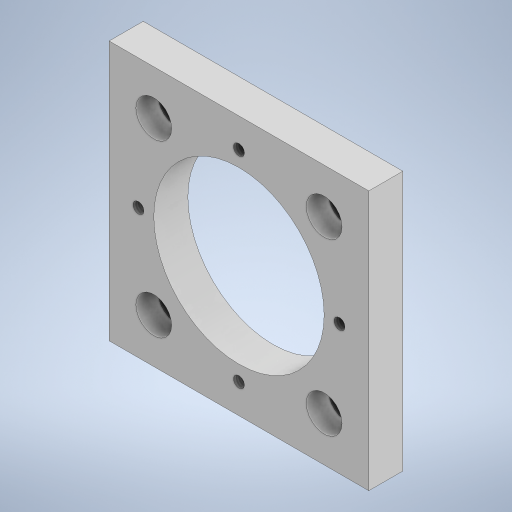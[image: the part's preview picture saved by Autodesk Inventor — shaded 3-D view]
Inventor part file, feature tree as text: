
AUTODESK INVENTOR PART (.ipt)
format: ipt  version: 2023 (Build 270158000, 158)  size: 272,896 bytes
history: native  units: mm
features: sketch x3, hole x2, projected_geometry x2, extrude x1
ambient origin geometry x8: Origin, YZ Plane, XZ Plane, XY Plane, X Axis, Y Axis, Z Axis, Center Point
bodies: Solid1 (feature_tree)
feature tree (8):
  extrude  "Extrusion1"  Depth=76.2mm
  hole  "Hole1"  [1 undecoded]
  hole  "Hole2"  [1 undecoded]
  sketch  "Sketch1"  dims[d0=76.2mm d1=76.2mm]
  sketch  "Sketch2"  dims[d2=10.0mm d3=0.0mm d4=50.0mm]
  projected_geometry  "Projected Loop1"
  sketch  "Sketch3"  dims[d5=50.0mm d6=6.0mm d7=12.7mm d8=10.5mm d9=6.5mm d10=90.0deg d11=8.0mm d12=20.594885mm d13=50.0mm d14=59.0mm d15=3.242mm d16=8.0mm d17=10.5mm d18=6.5mm d19=90.0deg d20=8.0mm d21=20.594885mm]
  projected_geometry  "Projected Loop2"
note: 2 required parameter values undecoded (feature->parameter linkage not recoverable at this tier; creation-order binding heuristic only, values carry confidence <= 0.55)
